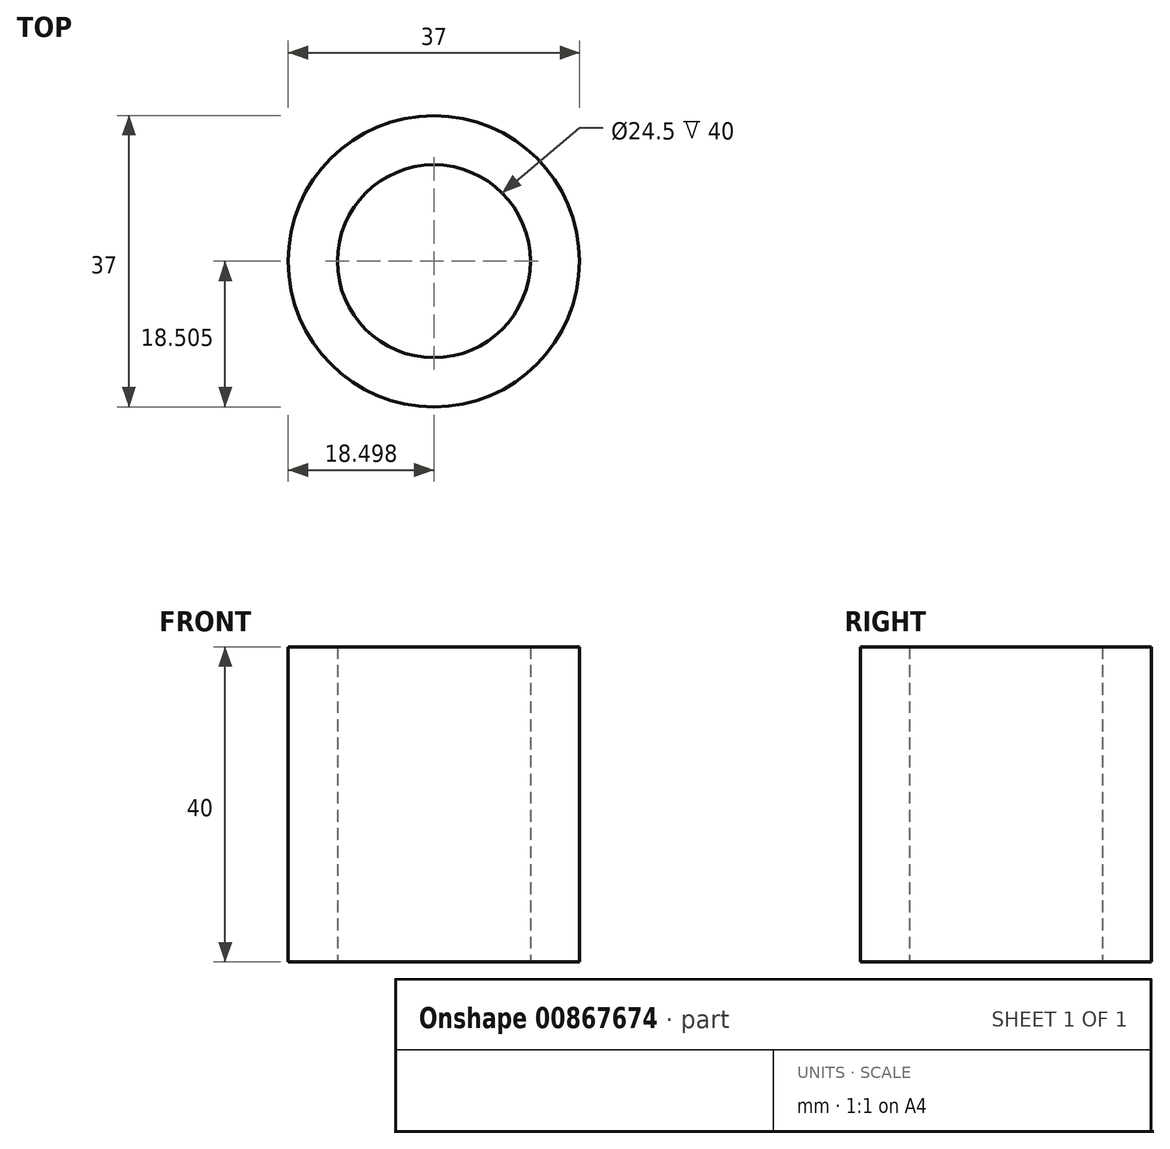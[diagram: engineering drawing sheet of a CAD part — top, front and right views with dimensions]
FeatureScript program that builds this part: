
annotation { "Feature Type Name" : "Feature", "Feature Type Description" : "" }
export const myFeature = defineFeature(function(context is Context, id is Id, definition is map)
    precondition{}
    {
        {
            var Q0;
            Q0=qCreatedBy(makeId("Top.planeOp"),FACE);
            var sketch = newSketch(context, id + "F0", { "sketchPlane" : qUnion([Q0])});
            skCircle(sketch, "E0", {"center": v(-15.16, 15.27) * mm, "radius": 18.5 * mm});
            skCircle(sketch, "E1", {"center": v(-15.16, 15.27) * mm, "radius": 12.25 * mm});
            skSolve(sketch);
        }
        {
            var Q0;
            Q0 = qSketchRegion(id + "F0", true);
            extrude(context, id + "F1", {"entities" : qUnion([Q0]), "depth" : 40 * mm, "offsetDistance" : 25 * mm});
        }
    });
